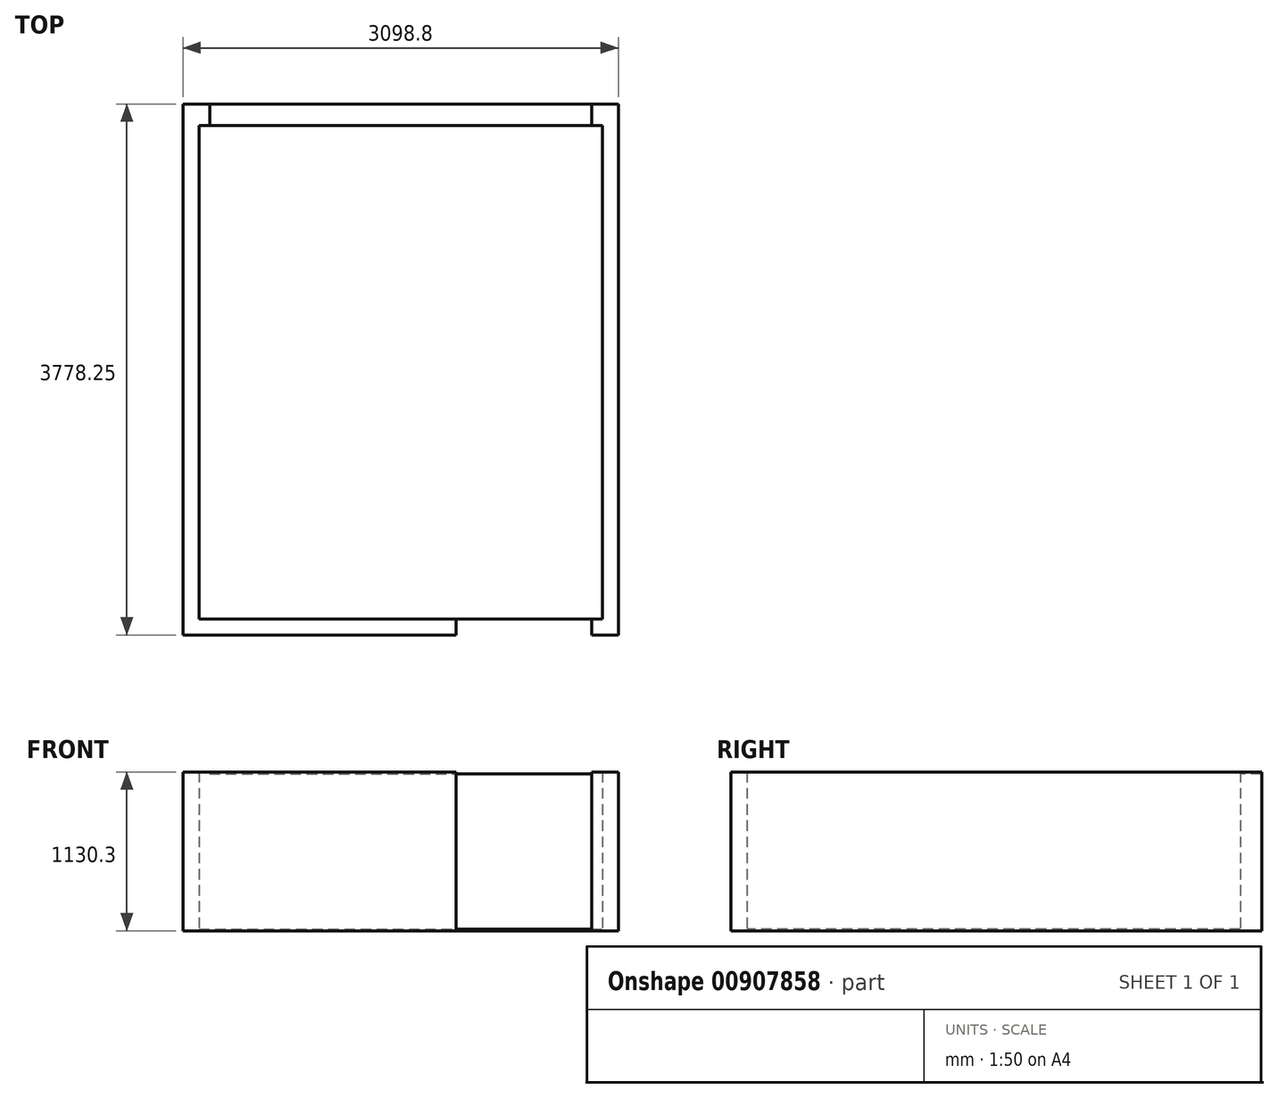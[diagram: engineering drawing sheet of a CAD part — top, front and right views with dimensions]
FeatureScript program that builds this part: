
annotation { "Feature Type Name" : "Feature", "Feature Type Description" : "" }
export const myFeature = defineFeature(function(context is Context, id is Id, definition is map)
    precondition{}
    {
        {
            var Q0;
            Q0=qCreatedBy(makeId("Top.planeOp"),FACE);
            var sketch = newSketch(context, id + "F0", { "sketchPlane" : qUnion([Q0])});
            skLineSegment(sketch, "E0", {"start": v(0, 3778.25) * mm, "end": v(3098.8, 3778.25) * mm});
            skLineSegment(sketch, "E1.3", {"start": v(114.3, 3625.85) * mm, "end": v(2984.5, 3625.85) * mm});
            skLineSegment(sketch, "E2.left", {"start": v(0, 3778.25) * mm, "end": v(0, 0) * mm});
            skLineSegment(sketch, "E2.right", {"start": v(114.3, 3625.85) * mm, "end": v(114.3, 114.3) * mm});
            skLineSegment(sketch, "E3.bottom", {"start": v(190.5, 3778.25) * mm, "end": v(2908.3, 3778.25) * mm});
            skLineSegment(sketch, "E3.top", {"start": v(190.5, 3625.85) * mm, "end": v(2908.3, 3625.85) * mm});
            skLineSegment(sketch, "E3.left", {"start": v(190.5, 3778.25) * mm, "end": v(190.5, 3625.85) * mm});
            skLineSegment(sketch, "E3.right", {"start": v(2908.3, 3778.25) * mm, "end": v(2908.3, 3625.85) * mm});
            skLineSegment(sketch, "E4.left", {"start": v(2984.5, 3625.85) * mm, "end": v(2984.5, 114.3) * mm});
            skLineSegment(sketch, "E4.right", {"start": v(3098.8, 3778.25) * mm, "end": v(3098.8, 0) * mm});
            skLineSegment(sketch, "E5.trimOffspring", {"start": v(114.3, 114.3) * mm, "end": v(2984.5, 114.3) * mm});
            skLineSegment(sketch, "E6.trimOffspring", {"start": v(0, 0) * mm, "end": v(3098.8, 0) * mm});
            skLineSegment(sketch, "E7.bottom", {"start": v(1943.1, 114.3) * mm, "end": v(2908.3, 114.3) * mm});
            skLineSegment(sketch, "E7.top", {"start": v(1943.1, 0) * mm, "end": v(2908.3, 0) * mm});
            skLineSegment(sketch, "E7.left", {"start": v(1943.1, 114.3) * mm, "end": v(1943.1, 0) * mm});
            skLineSegment(sketch, "E7.right", {"start": v(2908.3, 114.3) * mm, "end": v(2908.3, 0) * mm});
            skSolve(sketch);
        }
        {
            var Q0;
            {var subQ5=sQuery(id+"F0.wireOp",EDGE,"E2.left");Q0=makeQuery(id+"F0.imprint","IMPRINT",FACE,{"disambiguationData":[TD([[makeQuery(id+"F0.imprint","IMPRINT",EDGE,{"derivedFrom":subQ5}),1.0]])]});}
            var Q1;
            {var subQ0=sQuery(id+"F0.wireOp",EDGE,"E3.left");Q1=makeQuery(id+"F0.imprint","IMPRINT",FACE,{"disambiguationData":[TD([[makeQuery(id+"F0.imprint","IMPRINT",EDGE,{"derivedFrom":subQ0}),1.0]])]});}
            var Q2;
            {var subQ0=sQuery(id+"F0.wireOp",EDGE,"E3.right");Q2=makeQuery(id+"F0.imprint","IMPRINT",FACE,{"disambiguationData":[TD([[makeQuery(id+"F0.imprint","IMPRINT",EDGE,{"derivedFrom":subQ0}),1.0]])]});}
            var Q3;
            {var subQ0=sQuery(id+"F0.wireOp",EDGE,"E7.left");Q3=makeQuery(id+"F0.imprint","IMPRINT",FACE,{"disambiguationData":[TD([[makeQuery(id+"F0.imprint","IMPRINT",EDGE,{"derivedFrom":subQ0}),1.0]])]});}
            extrude(context, id + "F1", {"entities" : qUnion([Q0, Q1, Q2, Q3]), "depth" : 1117.6 * mm, "offsetDistance" : 25.4 * mm});
        }
        {
            var Q0;
            {var subQ0=sQuery(id+"F0.wireOp",EDGE,"E2.right");Q0=makeQuery(id+"F0.imprint","IMPRINT",FACE,{"disambiguationData":[TD([[makeQuery(id+"F0.imprint","IMPRINT",EDGE,{"derivedFrom":subQ0}),1.0]])]});}
            var Q1;
            Q1=makeQuery(id+"F1.opExtrude","CAP_FACE",FACE,{"disambiguationData":[OSD([sQuery(id+"F0.wireOp",EDGE,"E0"),sQuery(id+"F0.wireOp",EDGE,"E1.3"),sQuery(id+"F0.wireOp",EDGE,"E2.left"),sQuery(id+"F0.wireOp",EDGE,"E2.right"),sQuery(id+"F0.wireOp",EDGE,"E4.left"),sQuery(id+"F0.wireOp",EDGE,"E4.right"),sQuery(id+"F0.wireOp",EDGE,"E5.trimOffspring"),sQuery(id+"F0.wireOp",EDGE,"E6.trimOffspring")])],"isStart":false});
            extrude(context, id + "F2", {"entities" : qUnion([Q0, Q1]), "operationType" : NewBodyOperationType.ADD, "depth" : 12.7 * mm, "offsetDistance" : 25.4 * mm});
        }
        {
            var Q0;
            {var subQ0=sQuery(id+"F0.wireOp",EDGE,"E3.left");Q0=makeQuery(id+"F0.imprint","IMPRINT",FACE,{"disambiguationData":[TD([[makeQuery(id+"F0.imprint","IMPRINT",EDGE,{"derivedFrom":subQ0}),1.0]])]});}
            extrude(context, id + "F3", {"entities" : qUnion([Q0]), "operationType" : NewBodyOperationType.REMOVE, "depth" : 2387.6 * mm, "offsetDistance" : 25.4 * mm});
        }
        {
            var Q0;
            Q0=makeQuery(id+"F0.imprint","IMPRINT",FACE,{"disambiguationData":[TD([[makeQuery(id+"F0.imprint","IMPRINT",EDGE,{"derivedFrom":sQuery(id+"F0.wireOp",EDGE,"0a2b43e2-1613-46b9-b01d-519e5bdc8d04.bottom")}),-1.0]])]});
            var Q1;
            Q1=makeQuery(id+"F0.imprint","IMPRINT",FACE,{"disambiguationData":[TD([[makeQuery(id+"F0.imprint","IMPRINT",EDGE,{"derivedFrom":sQuery(id+"F0.wireOp",EDGE,"75dbd956-95aa-468a-bc59-f2c7192250f2.bottom")}),-1.0]])]});
            var Q2;
            Q2=makeQuery(id+"F0.imprint","IMPRINT",FACE,{"disambiguationData":[TD([[makeQuery(id+"F0.imprint","IMPRINT",EDGE,{"derivedFrom":sQuery(id+"F0.wireOp",EDGE,"31527499-7683-49db-8654-bf377255ae12.bottom")}),-1.0]])]});
            var Q3;
            Q3=makeQuery(id+"F0.imprint","IMPRINT",FACE,{"disambiguationData":[TD([[makeQuery(id+"F0.imprint","IMPRINT",EDGE,{"derivedFrom":sQuery(id+"F0.wireOp",EDGE,"7665eeba-05bf-4af7-ab7b-b7b8fc57c650.bottom")}),-1.0]])]});
            var Q4;
            Q4=makeQuery(id+"F0.imprint","IMPRINT",FACE,{"disambiguationData":[TD([[makeQuery(id+"F0.imprint","IMPRINT",EDGE,{"derivedFrom":sQuery(id+"F0.wireOp",EDGE,"bf809945-97a4-4754-b57b-1173dd48a5d4.bottom")}),-1.0]])]});
            var Q5;
            Q5=makeQuery(id+"F0.imprint","IMPRINT",FACE,{"disambiguationData":[TD([[makeQuery(id+"F0.imprint","IMPRINT",EDGE,{"derivedFrom":sQuery(id+"F0.wireOp",EDGE,"chDwJ9Im-fMP2-oQeb-cNXz-O2Ukgx9ftVdQ.bottom")}),-1.0]])]});
            var Q6;
            Q6=makeQuery(id+"F0.imprint","IMPRINT",FACE,{"disambiguationData":[TD([[makeQuery(id+"F0.imprint","IMPRINT",EDGE,{"derivedFrom":sQuery(id+"F0.wireOp",EDGE,"d9bad6fb-0d31-4a17-a9a1-20050558bc9c.bottom")}),-1.0]])]});
            var Q7;
            Q7=makeQuery(id+"F0.imprint","IMPRINT",FACE,{"disambiguationData":[TD([[makeQuery(id+"F0.imprint","IMPRINT",EDGE,{"derivedFrom":sQuery(id+"F0.wireOp",EDGE,"cdddc103-8771-45dc-85b7-91cd35213936.bottom")}),-1.0]])]});
            var Q8;
            Q8=makeQuery(id+"F0.imprint","IMPRINT",FACE,{"disambiguationData":[TD([[makeQuery(id+"F0.imprint","IMPRINT",EDGE,{"derivedFrom":sQuery(id+"F0.wireOp",EDGE,"fb0b1036-373d-4fd0-96ec-70b4ccf50ddf.bottom")}),-1.0]])]});
            var Q9;
            {var subQ0=sQuery(id+"F0.wireOp",EDGE,"E3.left");Q9=makeQuery(id+"F0.imprint","IMPRINT",FACE,{"disambiguationData":[TD([[makeQuery(id+"F0.imprint","IMPRINT",EDGE,{"derivedFrom":subQ0}),1.0]])]});}
            var Q10;
            Q10=makeQuery(id+"F0.imprint","IMPRINT",FACE,{"disambiguationData":[TD([[makeQuery(id+"F0.imprint","IMPRINT",EDGE,{"derivedFrom":sQuery(id+"F0.wireOp",EDGE,"868d5200-31d1-4bc4-b75b-16b42e1032bf.bottom")}),-1.0]])]});
            var Q11;
            Q11=makeQuery(id+"F0.imprint","IMPRINT",FACE,{"disambiguationData":[TD([[makeQuery(id+"F0.imprint","IMPRINT",EDGE,{"derivedFrom":sQuery(id+"F0.wireOp",EDGE,"0b90646e-e787-4eb4-9473-c4e5a2be35a3.bottom")}),-1.0]])]});
            var Q12;
            Q12=makeQuery(id+"F0.imprint","IMPRINT",FACE,{"disambiguationData":[TD([[makeQuery(id+"F0.imprint","IMPRINT",EDGE,{"derivedFrom":sQuery(id+"F0.wireOp",EDGE,"2888c67e-b885-45bf-84c9-a484d7bfb063.bottom")}),-1.0]])]});
            var Q13;
            {var subQ0=sQuery(id+"F0.wireOp",EDGE,"d5cb1f5a-13c6-4258-9805-51efdfbb26c0.left");Q13=makeQuery(id+"F0.imprint","IMPRINT",FACE,{"disambiguationData":[TD([[makeQuery(id+"F0.imprint","IMPRINT",EDGE,{"derivedFrom":subQ0}),1.0]])]});}
            var Q14;
            {var subQ0=sQuery(id+"F0.wireOp",EDGE,"cd29d22e-5f8b-421e-897b-4e4b0b2e9ef4.left");Q14=makeQuery(id+"F0.imprint","IMPRINT",FACE,{"disambiguationData":[TD([[makeQuery(id+"F0.imprint","IMPRINT",EDGE,{"derivedFrom":subQ0}),1.0]])]});}
            var Q15;
            {var subQ0=sQuery(id+"F0.wireOp",EDGE,"530c1226-43a9-4f3c-8756-0bf111c428e1.left");Q15=makeQuery(id+"F0.imprint","IMPRINT",FACE,{"disambiguationData":[TD([[makeQuery(id+"F0.imprint","IMPRINT",EDGE,{"derivedFrom":subQ0}),1.0]])]});}
            var Q16;
            {var subQ0=sQuery(id+"F0.wireOp",EDGE,"51cbba4f-cedb-4130-a4d2-46d0b5f2c4eb.left");Q16=makeQuery(id+"F0.imprint","IMPRINT",FACE,{"disambiguationData":[TD([[makeQuery(id+"F0.imprint","IMPRINT",EDGE,{"derivedFrom":subQ0}),1.0]])]});}
            var Q17;
            {var subQ0=sQuery(id+"F0.wireOp",EDGE,"f8b0682a-8219-4b9c-8f4b-9958931c9df1.left");Q17=makeQuery(id+"F0.imprint","IMPRINT",FACE,{"disambiguationData":[TD([[makeQuery(id+"F0.imprint","IMPRINT",EDGE,{"derivedFrom":subQ0}),1.0]])]});}
            var Q18;
            Q18=makeQuery(id+"F0.imprint","IMPRINT",FACE,{"disambiguationData":[TD([[makeQuery(id+"F0.imprint","IMPRINT",EDGE,{"derivedFrom":sQuery(id+"F0.wireOp",EDGE,"a3c2858f-9076-4590-b338-f6be4b95bc3e.bottom")}),-1.0]])]});
            var Q19;
            Q19=makeQuery(id+"F0.imprint","IMPRINT",FACE,{"disambiguationData":[TD([[makeQuery(id+"F0.imprint","IMPRINT",EDGE,{"derivedFrom":sQuery(id+"F0.wireOp",EDGE,"9dc2cd4a-ec81-43c2-b85f-240c602b41df.bottom")}),-1.0]])]});
            var Q20;
            Q20=makeQuery(id+"F0.imprint","IMPRINT",FACE,{"disambiguationData":[TD([[makeQuery(id+"F0.imprint","IMPRINT",EDGE,{"derivedFrom":sQuery(id+"F0.wireOp",EDGE,"edaaddad-d76f-4b76-a45a-14b1fc3aa481.bottom")}),-1.0]])]});
            var Q21;
            Q21=makeQuery(id+"F0.imprint","IMPRINT",FACE,{"disambiguationData":[TD([[makeQuery(id+"F0.imprint","IMPRINT",EDGE,{"derivedFrom":sQuery(id+"F0.wireOp",EDGE,"9b46e30d-555b-46f0-a5fb-fab40dc90f03.bottom")}),-1.0]])]});
            var Q22;
            Q22=makeQuery(id+"F0.imprint","IMPRINT",FACE,{"disambiguationData":[TD([[makeQuery(id+"F0.imprint","IMPRINT",EDGE,{"derivedFrom":sQuery(id+"F0.wireOp",EDGE,"24dcbd9a-6578-4ece-966a-f071d542d0fb.bottom")}),-1.0]])]});
            var Q23;
            Q23=makeQuery(id+"F0.imprint","IMPRINT",FACE,{"disambiguationData":[TD([[makeQuery(id+"F0.imprint","IMPRINT",EDGE,{"derivedFrom":sQuery(id+"F0.wireOp",EDGE,"ca3c58e5-e312-4de2-8add-c19eeb1c795a.bottom")}),-1.0]])]});
            var Q24;
            Q24=makeQuery(id+"F0.imprint","IMPRINT",FACE,{"disambiguationData":[TD([[makeQuery(id+"F0.imprint","IMPRINT",EDGE,{"derivedFrom":sQuery(id+"F0.wireOp",EDGE,"d7c3f322-1db2-4d8d-87b1-6d43f8c2f2ea.bottom")}),-1.0]])]});
            var Q25;
            Q25=makeQuery(id+"F0.imprint","IMPRINT",FACE,{"disambiguationData":[TD([[makeQuery(id+"F0.imprint","IMPRINT",EDGE,{"derivedFrom":sQuery(id+"F0.wireOp",EDGE,"c570d550-490a-41cf-af55-43bf55c69d60.bottom")}),-1.0]])]});
            var Q26;
            Q26=makeQuery(id+"F0.imprint","IMPRINT",FACE,{"disambiguationData":[TD([[makeQuery(id+"F0.imprint","IMPRINT",EDGE,{"derivedFrom":sQuery(id+"F0.wireOp",EDGE,"9a2625cd-0bf7-4f54-a3fc-6b036aaad3f3.bottom")}),-1.0]])]});
            var Q27;
            Q27=makeQuery(id+"F0.imprint","IMPRINT",FACE,{"disambiguationData":[TD([[makeQuery(id+"F0.imprint","IMPRINT",EDGE,{"derivedFrom":sQuery(id+"F0.wireOp",EDGE,"2aac8ed0-74eb-46e2-bf13-b2b71686aa77.bottom")}),-1.0]])]});
            var Q28;
            Q28=makeQuery(id+"F0.imprint","IMPRINT",FACE,{"disambiguationData":[TD([[makeQuery(id+"F0.imprint","IMPRINT",EDGE,{"derivedFrom":sQuery(id+"F0.wireOp",EDGE,"b20b78d1-5675-47cb-bab8-026e02f0d24b.bottom")}),-1.0]])]});
            var Q29;
            Q29=makeQuery(id+"F0.imprint","IMPRINT",FACE,{"disambiguationData":[TD([[makeQuery(id+"F0.imprint","IMPRINT",EDGE,{"derivedFrom":sQuery(id+"F0.wireOp",EDGE,"ac199946-13ef-4769-a847-0e5d73b6242f.bottom")}),-1.0]])]});
            var Q30;
            Q30=makeQuery(id+"F0.imprint","IMPRINT",FACE,{"disambiguationData":[TD([[makeQuery(id+"F0.imprint","IMPRINT",EDGE,{"derivedFrom":sQuery(id+"F0.wireOp",EDGE,"d0a596df-7eb1-49b6-aad0-5788527a46ed.bottom")}),-1.0]])]});
            extrude(context, id + "F4", {"entities" : qUnion([Q0, Q1, Q2, Q3, Q4, Q5, Q6, Q7, Q8, Q9, Q10, Q11, Q12, Q13, Q14, Q15, Q16, Q17, Q18, Q19, Q20, Q21, Q22, Q23, Q24, Q25, Q26, Q27, Q28, Q29, Q30]), "operationType" : NewBodyOperationType.ADD, "depth" : 1117.6 * mm, "offsetDistance" : 25.4 * mm});
        }
        {
            var Q0;
            Q0=makeQuery(id+"F0.imprint","IMPRINT",FACE,{"disambiguationData":[TD([[makeQuery(id+"F0.imprint","IMPRINT",EDGE,{"derivedFrom":sQuery(id+"F0.wireOp",EDGE,"jPPJHqI0-KoZ3-GDFn-ihlH-owTmKjjl9Qax.bottom")}),-1.0]])]});
            var Q1;
            Q1=makeQuery(id+"F0.imprint","IMPRINT",FACE,{"disambiguationData":[TD([[makeQuery(id+"F0.imprint","IMPRINT",EDGE,{"derivedFrom":sQuery(id+"F0.wireOp",EDGE,"ea3e5e94-8b17-4bc4-8dd4-1a3eefd05c6c.bottom")}),-1.0]])]});
            var Q2;
            Q2=makeQuery(id+"F0.imprint","IMPRINT",FACE,{"disambiguationData":[TD([[makeQuery(id+"F0.imprint","IMPRINT",EDGE,{"derivedFrom":sQuery(id+"F0.wireOp",EDGE,"ecd1f5cf-6dff-4b43-9028-2be6698a62c8.bottom")}),-1.0]])]});
            var Q3;
            Q3=makeQuery(id+"F0.imprint","IMPRINT",FACE,{"disambiguationData":[TD([[makeQuery(id+"F0.imprint","IMPRINT",EDGE,{"derivedFrom":sQuery(id+"F0.wireOp",EDGE,"f931fbda-3326-4e22-9a92-4bf93f78eda6.bottom")}),-1.0]])]});
            var Q4;
            Q4=makeQuery(id+"F0.imprint","IMPRINT",FACE,{"disambiguationData":[TD([[makeQuery(id+"F0.imprint","IMPRINT",EDGE,{"derivedFrom":sQuery(id+"F0.wireOp",EDGE,"41a76476-aefd-491f-9f96-ed514717fb2d.bottom")}),-1.0]])]});
            var Q5;
            Q5=makeQuery(id+"F0.imprint","IMPRINT",FACE,{"disambiguationData":[TD([[makeQuery(id+"F0.imprint","IMPRINT",EDGE,{"derivedFrom":sQuery(id+"F0.wireOp",EDGE,"b1809bc7-11ed-485d-9c23-af9fbcd34c33.bottom")}),-1.0]])]});
            var Q6;
            Q6=makeQuery(id+"F0.imprint","IMPRINT",FACE,{"disambiguationData":[TD([[makeQuery(id+"F0.imprint","IMPRINT",EDGE,{"derivedFrom":sQuery(id+"F0.wireOp",EDGE,"ab5d99dd-845a-423d-85f9-8ae4ebad44d7.bottom")}),-1.0]])]});
            var Q7;
            Q7=makeQuery(id+"F0.imprint","IMPRINT",FACE,{"disambiguationData":[TD([[makeQuery(id+"F0.imprint","IMPRINT",EDGE,{"derivedFrom":sQuery(id+"F0.wireOp",EDGE,"8b9a9ae4-81e4-48ab-b23d-b49280d3722b.bottom")}),-1.0]])]});
            var Q8;
            Q8=makeQuery(id+"F0.imprint","IMPRINT",FACE,{"disambiguationData":[TD([[makeQuery(id+"F0.imprint","IMPRINT",EDGE,{"derivedFrom":sQuery(id+"F0.wireOp",EDGE,"628cb0c7-a52e-4326-abc9-0be708525ed1.bottom")}),-1.0]])]});
            var Q9;
            {var subQ0=sQuery(id+"F0.wireOp",EDGE,"E7.left");Q9=makeQuery(id+"F0.imprint","IMPRINT",FACE,{"disambiguationData":[TD([[makeQuery(id+"F0.imprint","IMPRINT",EDGE,{"derivedFrom":subQ0}),1.0]])]});}
            var Q10;
            Q10=makeQuery(id+"F0.imprint","IMPRINT",FACE,{"disambiguationData":[TD([[makeQuery(id+"F0.imprint","IMPRINT",EDGE,{"derivedFrom":sQuery(id+"F0.wireOp",EDGE,"9046df1a-b07b-4f4d-8778-30d9371e47b7.bottom")}),-1.0]])]});
            var Q11;
            Q11=makeQuery(id+"F0.imprint","IMPRINT",FACE,{"disambiguationData":[TD([[makeQuery(id+"F0.imprint","IMPRINT",EDGE,{"derivedFrom":sQuery(id+"F0.wireOp",EDGE,"b4e37ac2-bf45-407d-9ce5-2fc7d110be35.bottom")}),-1.0]])]});
            var Q12;
            Q12=makeQuery(id+"F0.imprint","IMPRINT",FACE,{"disambiguationData":[TD([[makeQuery(id+"F0.imprint","IMPRINT",EDGE,{"derivedFrom":sQuery(id+"F0.wireOp",EDGE,"477ff269-766b-4fbe-96c7-b09697e98b7a.bottom")}),-1.0]])]});
            var Q13;
            Q13=makeQuery(id+"F0.imprint","IMPRINT",FACE,{"disambiguationData":[TD([[makeQuery(id+"F0.imprint","IMPRINT",EDGE,{"derivedFrom":sQuery(id+"F0.wireOp",EDGE,"8df5f852-ae67-4e94-b68b-5095b8b4696b.bottom")}),-1.0]])]});
            var Q14;
            Q14=makeQuery(id+"F0.imprint","IMPRINT",FACE,{"disambiguationData":[TD([[makeQuery(id+"F0.imprint","IMPRINT",EDGE,{"derivedFrom":sQuery(id+"F0.wireOp",EDGE,"32fd72dc-0daa-4c70-a71d-8836f0894e82.bottom")}),-1.0]])]});
            var Q15;
            Q15=makeQuery(id+"F0.imprint","IMPRINT",FACE,{"disambiguationData":[TD([[makeQuery(id+"F0.imprint","IMPRINT",EDGE,{"derivedFrom":sQuery(id+"F0.wireOp",EDGE,"348489a9-a8a7-40bc-8c03-01cf3d2c3209.bottom")}),-1.0]])]});
            var Q16;
            Q16=makeQuery(id+"F0.imprint","IMPRINT",FACE,{"disambiguationData":[TD([[makeQuery(id+"F0.imprint","IMPRINT",EDGE,{"derivedFrom":sQuery(id+"F0.wireOp",EDGE,"7fe46254-8236-43be-90c8-a025c9408aa3.bottom")}),-1.0]])]});
            var Q17;
            Q17=makeQuery(id+"F0.imprint","IMPRINT",FACE,{"disambiguationData":[TD([[makeQuery(id+"F0.imprint","IMPRINT",EDGE,{"derivedFrom":sQuery(id+"F0.wireOp",EDGE,"c8a50ba2-e5f2-4bf9-b18d-3bd799b098a9.bottom")}),-1.0]])]});
            var Q18;
            Q18=makeQuery(id+"F0.imprint","IMPRINT",FACE,{"disambiguationData":[TD([[makeQuery(id+"F0.imprint","IMPRINT",EDGE,{"derivedFrom":sQuery(id+"F0.wireOp",EDGE,"dc274b57-7786-4da9-a7b2-7d64197c8299.bottom")}),-1.0]])]});
            var Q19;
            Q19=makeQuery(id+"F0.imprint","IMPRINT",FACE,{"disambiguationData":[TD([[makeQuery(id+"F0.imprint","IMPRINT",EDGE,{"derivedFrom":sQuery(id+"F0.wireOp",EDGE,"ced0d626-5882-4a4c-840c-23ec407a28b1.bottom")}),-1.0]])]});
            var Q20;
            Q20=makeQuery(id+"F0.imprint","IMPRINT",FACE,{"disambiguationData":[TD([[makeQuery(id+"F0.imprint","IMPRINT",EDGE,{"derivedFrom":sQuery(id+"F0.wireOp",EDGE,"4e508893-1a30-48ee-9e72-011e416d27be.bottom")}),-1.0]])]});
            var Q21;
            Q21=makeQuery(id+"F0.imprint","IMPRINT",FACE,{"disambiguationData":[TD([[makeQuery(id+"F0.imprint","IMPRINT",EDGE,{"derivedFrom":sQuery(id+"F0.wireOp",EDGE,"0b54b67d-aedd-4c25-b9c3-47f1fd7aec1a.bottom")}),-1.0]])]});
            var Q22;
            Q22=makeQuery(id+"F0.imprint","IMPRINT",FACE,{"disambiguationData":[TD([[makeQuery(id+"F0.imprint","IMPRINT",EDGE,{"derivedFrom":sQuery(id+"F0.wireOp",EDGE,"6250e88f-df8c-41e6-87eb-fde9335a9936.bottom")}),-1.0]])]});
            extrude(context, id + "F5", {"entities" : qUnion([Q0, Q1, Q2, Q3, Q4, Q5, Q6, Q7, Q8, Q9, Q10, Q11, Q12, Q13, Q14, Q15, Q16, Q17, Q18, Q19, Q20, Q21, Q22]), "operationType" : NewBodyOperationType.REMOVE, "depth" : 2159 * mm, "offsetDistance" : 25.4 * mm});
        }
    });
